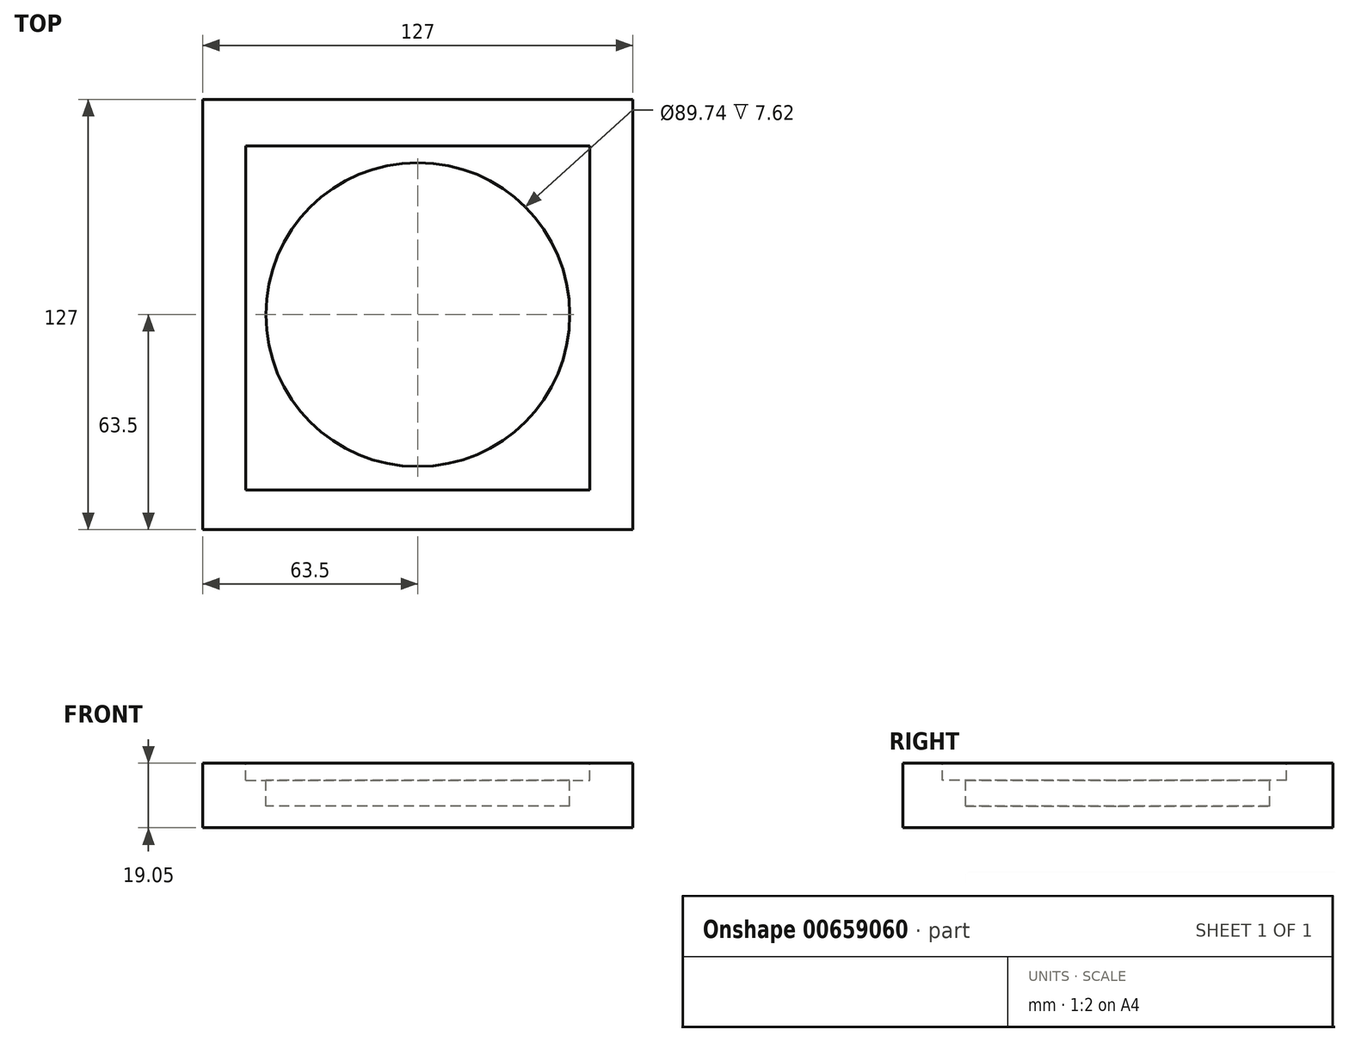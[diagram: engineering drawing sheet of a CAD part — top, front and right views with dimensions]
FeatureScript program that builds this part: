
annotation { "Feature Type Name" : "Feature", "Feature Type Description" : "" }
export const myFeature = defineFeature(function(context is Context, id is Id, definition is map)
    precondition{}
    {
        {
            var Q0;
            Q0=qCreatedBy(makeId("Top.planeOp"),FACE);
            var sketch = newSketch(context, id + "F0", { "sketchPlane" : qUnion([Q0])});
            skLineSegment(sketch, "E0.bottom", {"start": v(-63.5, 63.5) * mm, "end": v(63.5, 63.5) * mm});
            skLineSegment(sketch, "E0.top", {"start": v(-63.5, -63.5) * mm, "end": v(63.5, -63.5) * mm});
            skLineSegment(sketch, "E0.left", {"start": v(-63.5, 63.5) * mm, "end": v(-63.5, -63.5) * mm});
            skLineSegment(sketch, "E0.right", {"start": v(63.5, 63.5) * mm, "end": v(63.5, -63.5) * mm});
            skSolve(sketch);
        }
        {
            var Q0;
            Q0=makeQuery(id+"F0.imprint","IMPRINT",FACE,{"disambiguationData":[TD([[makeQuery(id+"F0.imprint","IMPRINT",EDGE,{"derivedFrom":sQuery(id+"F0.wireOp",EDGE,"E0.bottom")}),-1.0]])]});
            extrude(context, id + "F1", {"entities" : qUnion([Q0]), "depth" : 7.62 * mm, "offsetDistance" : 25.4 * mm});
        }
        {
            var Q0;
            Q0=makeQuery(id+"F1.opExtrude","CAP_FACE",FACE,{"disambiguationData":[OSD([sQuery(id+"F0.wireOp",EDGE,"E0.bottom"),sQuery(id+"F0.wireOp",EDGE,"E0.top"),sQuery(id+"F0.wireOp",EDGE,"E0.left"),sQuery(id+"F0.wireOp",EDGE,"E0.right")])],"isStart":false});
            var sketch = newSketch(context, id + "F2", { "sketchPlane" : qUnion([Q0])});
            skLineSegment(sketch, "E1.bottom", {"start": v(-63.5, 63.5) * mm, "end": v(63.5, 63.5) * mm});
            skLineSegment(sketch, "E1.top", {"start": v(-63.5, -63.5) * mm, "end": v(63.5, -63.5) * mm});
            skLineSegment(sketch, "E1.left", {"start": v(-63.5, 63.5) * mm, "end": v(-63.5, -63.5) * mm});
            skLineSegment(sketch, "E1.right", {"start": v(63.5, 63.5) * mm, "end": v(63.5, -63.5) * mm});
            skSolve(sketch);
        }
        {
            var Q0;
            Q0 = qSketchRegion(id + "F2", true);
            extrude(context, id + "F3", {"entities" : qUnion([Q0]), "operationType" : NewBodyOperationType.ADD, "depth" : 11.43 * mm, "offsetDistance" : 25.4 * mm});
        }
        {
            var Q0;
            Q0=makeQuery(id+"F3.opExtrude","CAP_FACE",FACE,{"disambiguationData":[OSD([sQuery(id+"F2.wireOp",EDGE,"E1.bottom"),sQuery(id+"F2.wireOp",EDGE,"E1.top"),sQuery(id+"F2.wireOp",EDGE,"E1.left"),sQuery(id+"F2.wireOp",EDGE,"E1.right")])],"isStart":false});
            var sketch = newSketch(context, id + "F4", { "sketchPlane" : qUnion([Q0])});
            skLineSegment(sketch, "E2.bottom", {"start": v(-50.8, 49.86) * mm, "end": v(50.8, 49.86) * mm});
            skLineSegment(sketch, "E2.top", {"start": v(-50.8, -51.74) * mm, "end": v(50.8, -51.74) * mm});
            skLineSegment(sketch, "E2.left", {"start": v(-50.8, 49.86) * mm, "end": v(-50.8, -51.74) * mm});
            skLineSegment(sketch, "E2.right", {"start": v(50.8, 49.86) * mm, "end": v(50.8, -51.74) * mm});
            skSolve(sketch);
        }
        {
            var Q0;
            Q0=makeQuery(id+"F4.imprint","IMPRINT",FACE,{"disambiguationData":[TD([[makeQuery(id+"F4.imprint","IMPRINT",EDGE,{"derivedFrom":sQuery(id+"F4.wireOp",EDGE,"E2.bottom")}),-1.0]])]});
            extrude(context, id + "F5", {"entities" : qUnion([Q0]), "operationType" : NewBodyOperationType.REMOVE, "oppositeDirection" : true, "depth" : 5.08 * mm, "offsetDistance" : 25.4 * mm});
        }
        {
            var Q0;
            Q0=makeQuery(id+"F5.boolean.opBoolean","COPY",FACE,{"derivedFrom":makeQuery(id+"F5.opExtrude","CAP_FACE",FACE,{"disambiguationData":[OSD([sQuery(id+"F4.wireOp",EDGE,"E2.bottom"),sQuery(id+"F4.wireOp",EDGE,"E2.top"),sQuery(id+"F4.wireOp",EDGE,"E2.left"),sQuery(id+"F4.wireOp",EDGE,"E2.right")])],"isStart":false})});
            var sketch = newSketch(context, id + "F6", { "sketchPlane" : qUnion([Q0])});
            skCircle(sketch, "E3", {"center": v(0, 0) * mm, "radius": 44.87 * mm});
            skSolve(sketch);
        }
        {
            var Q0;
            Q0 = qSketchRegion(id + "F6", true);
            extrude(context, id + "F7", {"entities" : qUnion([Q0]), "operationType" : NewBodyOperationType.REMOVE, "oppositeDirection" : true, "depth" : 7.62 * mm, "offsetDistance" : 25.4 * mm});
        }
    });
